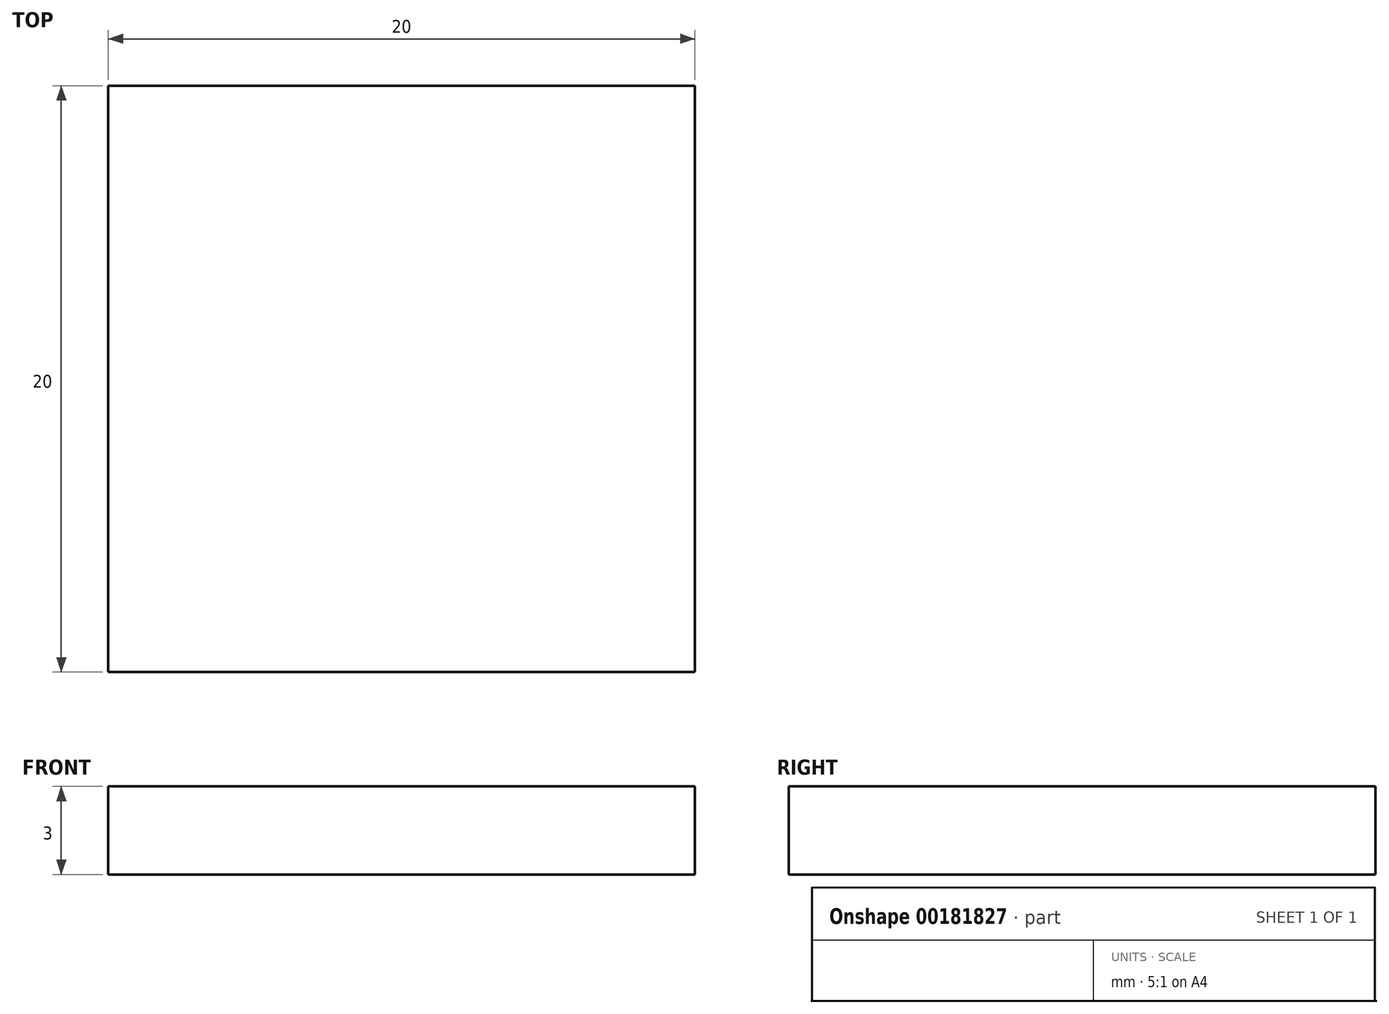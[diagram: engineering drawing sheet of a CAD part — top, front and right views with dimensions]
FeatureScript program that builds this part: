
annotation { "Feature Type Name" : "Feature", "Feature Type Description" : "" }
export const myFeature = defineFeature(function(context is Context, id is Id, definition is map)
    precondition{}
    {
        {
            var Q0;
            Q0=qCreatedBy(makeId("Top.planeOp"),FACE);
            var sketch = newSketch(context, id + "F0", { "sketchPlane" : qUnion([Q0])});
            skLineSegment(sketch, "E0.bottom", {"start": v(10, 10) * mm, "end": v(-10, 10) * mm});
            skLineSegment(sketch, "E0.top", {"start": v(10, -10) * mm, "end": v(-10, -10) * mm});
            skLineSegment(sketch, "E0.left", {"start": v(10, 10) * mm, "end": v(10, -10) * mm});
            skLineSegment(sketch, "E0.right", {"start": v(-10, 10) * mm, "end": v(-10, -10) * mm});
            skPoint(sketch, "E0.middle", {"position": v(0, 0) * mm});
            skSolve(sketch);
        }
        {
            var Q0;
            Q0 = qSketchRegion(id + "F0", true);
            extrude(context, id + "F1", {"entities" : qUnion([Q0]), "depth" : 3 * mm});
        }
    });
